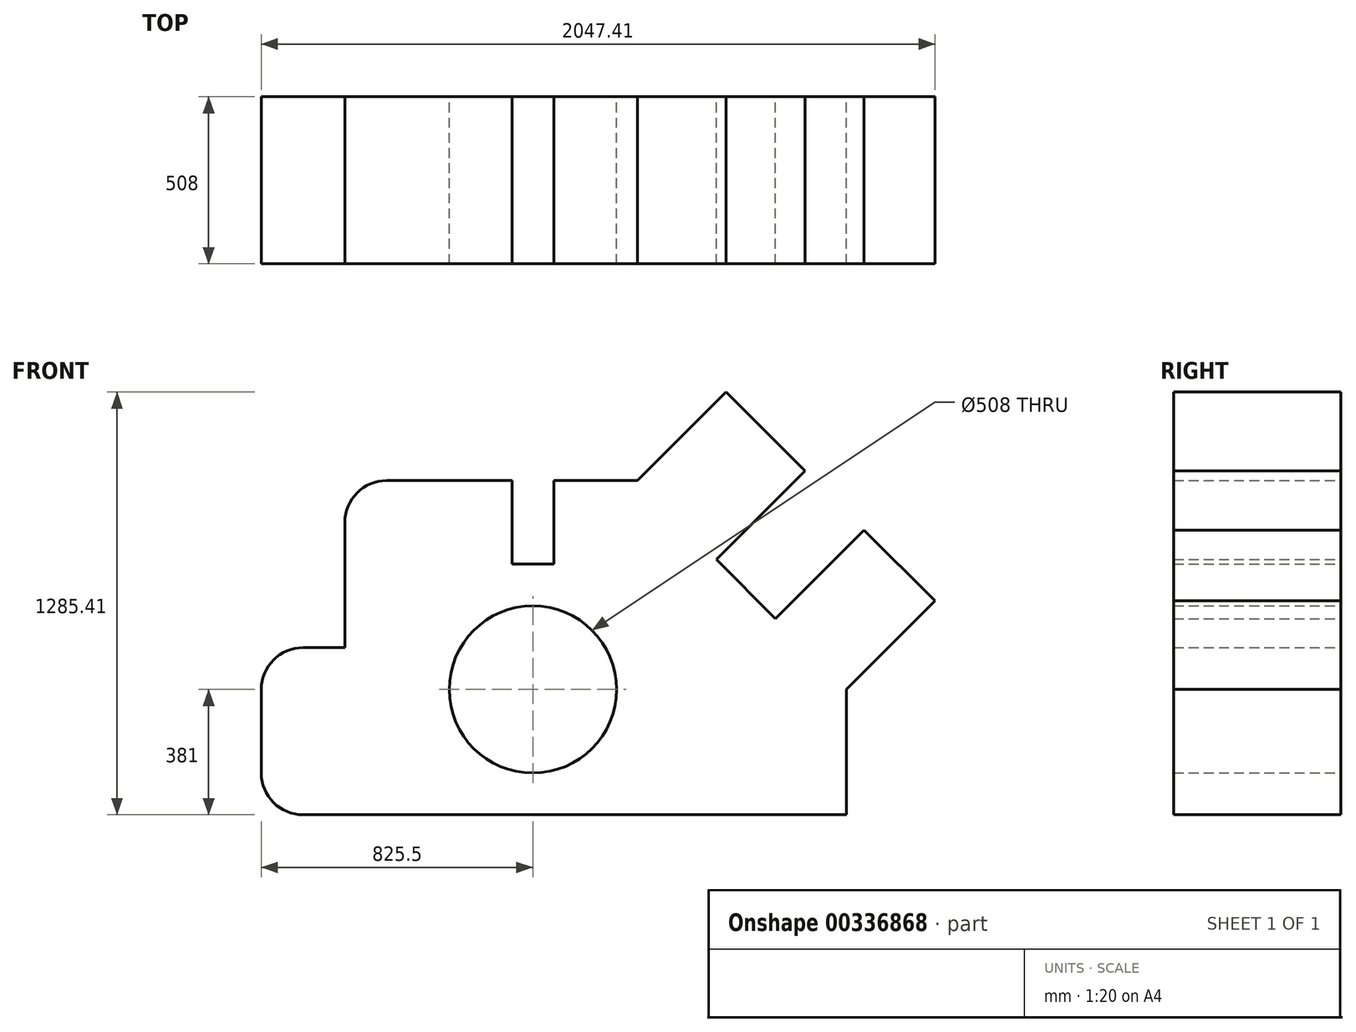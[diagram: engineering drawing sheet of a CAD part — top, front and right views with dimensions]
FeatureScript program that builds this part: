
annotation { "Feature Type Name" : "Feature", "Feature Type Description" : "" }
export const myFeature = defineFeature(function(context is Context, id is Id, definition is map)
    precondition{}
    {
        {
            var Q0;
            Q0=qCreatedBy(makeId("Front.planeOp"),FACE);
            var sketch = newSketch(context, id + "F0", { "sketchPlane" : qUnion([Q0])});
            skLineSegment(sketch, "E0", {"start": v(127, 0) * mm, "end": v(1778, 0) * mm});
            skLineSegment(sketch, "E1", {"start": v(1778, 0) * mm, "end": v(1778, 381) * mm});
            skLineSegment(sketch, "E2", {"start": v(1778, 381) * mm, "end": v(2047.4, 650.4) * mm});
            skLineSegment(sketch, "E3", {"start": v(2047.4, 650.4) * mm, "end": v(1831.88, 865.93) * mm});
            skLineSegment(sketch, "E4", {"start": v(1831.88, 865.93) * mm, "end": v(1562.47, 596.53) * mm});
            skLineSegment(sketch, "E5", {"start": v(1562.47, 596.53) * mm, "end": v(1382.87, 776.13) * mm});
            skLineSegment(sketch, "E6", {"start": v(1382.87, 776.13) * mm, "end": v(1652.28, 1045.54) * mm});
            skLineSegment(sketch, "E7", {"start": v(1652.28, 1045.54) * mm, "end": v(1412.4, 1285.4) * mm});
            skLineSegment(sketch, "E8", {"start": v(1412.4, 1285.4) * mm, "end": v(1143, 1016) * mm});
            skLineSegment(sketch, "E9", {"start": v(1143, 1016) * mm, "end": v(889, 1016) * mm});
            skLineSegment(sketch, "E10", {"start": v(889, 1016) * mm, "end": v(889, 762) * mm});
            skLineSegment(sketch, "E11", {"start": v(889, 762) * mm, "end": v(762, 762) * mm});
            skLineSegment(sketch, "E12", {"start": v(762, 762) * mm, "end": v(762, 1016) * mm});
            skLineSegment(sketch, "E13", {"start": v(762, 1016) * mm, "end": v(381, 1016) * mm});
            skLineSegment(sketch, "E14", {"start": v(254, 889) * mm, "end": v(254, 508) * mm});
            skLineSegment(sketch, "E15", {"start": v(0, 127) * mm, "end": v(0, 381) * mm});
            skLineSegment(sketch, "E16", {"start": v(254, 508) * mm, "end": v(127, 508) * mm});
            skCircle(sketch, "E17", {"center": v(825.5, 381) * mm, "radius": 254 * mm});
            skPoint(sketch, "E18.visualSharp", {"position": v(0, 508) * mm});
            skArc(sketch, "E18.filletArc", {"start": v(127, 508) * mm, "mid": v(37.2, 470.8) * mm, "end": v(0, 381) * mm});
            skPoint(sketch, "E19.visualSharp", {"position": v(0, 0) * mm});
            skArc(sketch, "E19.filletArc", {"start": v(0, 127) * mm, "mid": v(37.2, 37.2) * mm, "end": v(127, 0) * mm});
            skPoint(sketch, "E20.visualSharp", {"position": v(254, 1016) * mm});
            skArc(sketch, "E20.filletArc", {"start": v(381, 1016) * mm, "mid": v(291.2, 978.8) * mm, "end": v(254, 889) * mm});
            skSolve(sketch);
        }
        {
            var Q0;
            Q0=makeQuery(id+"F0.imprint","IMPRINT",FACE,{"disambiguationData":[TD([[makeQuery(id+"F0.imprint","IMPRINT",EDGE,{"derivedFrom":sQuery(id+"F0.wireOp",EDGE,"E0")}),1.0]])]});
            extrude(context, id + "F1", {"entities" : qUnion([Q0]), "depth" : 508 * mm});
        }
    });
